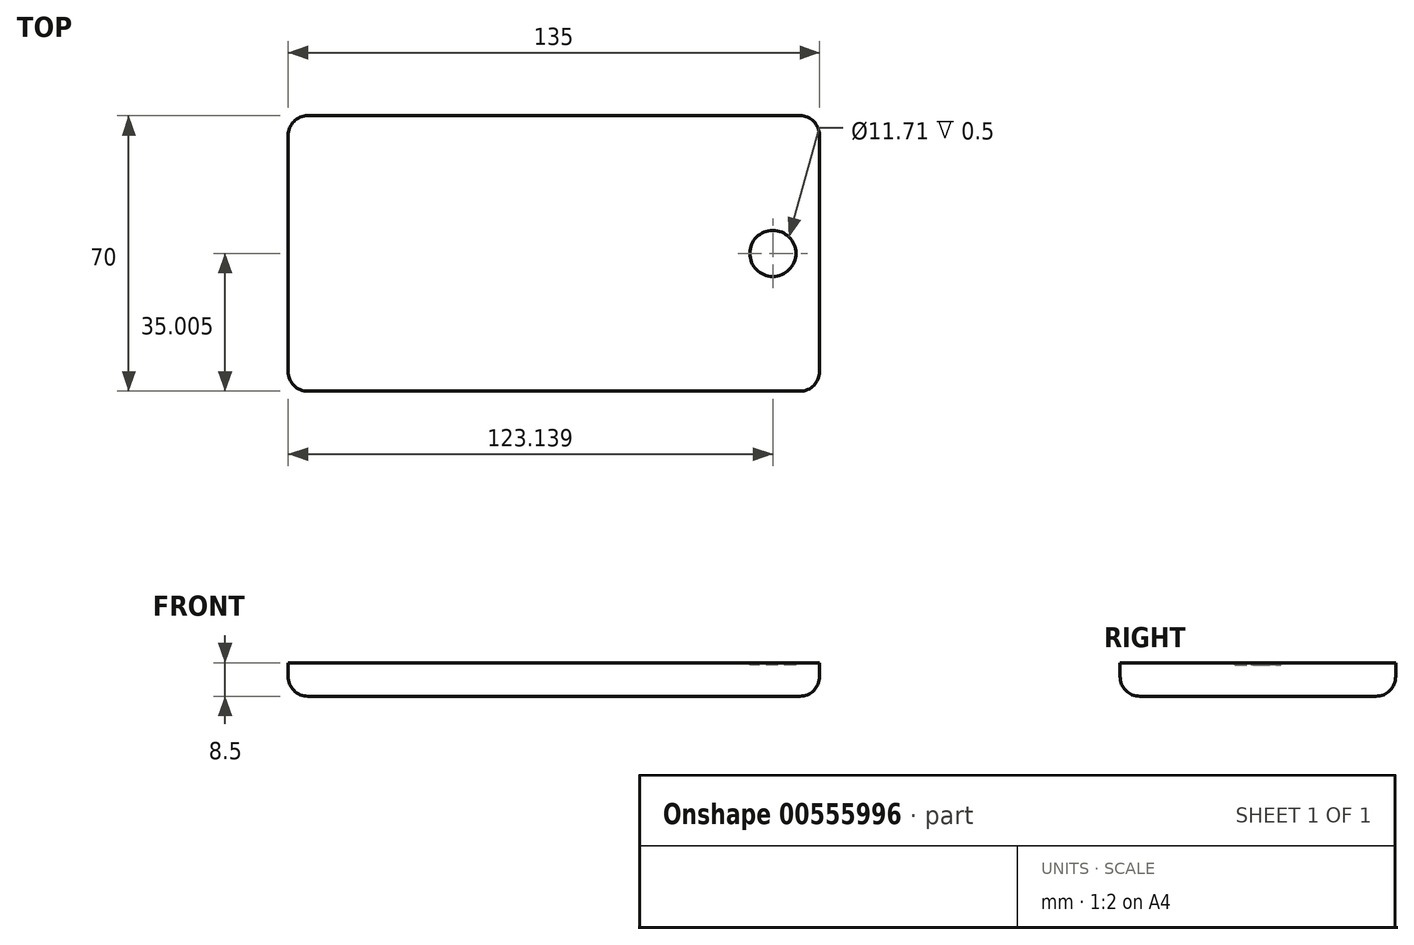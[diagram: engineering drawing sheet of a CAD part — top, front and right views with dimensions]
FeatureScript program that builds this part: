
annotation { "Feature Type Name" : "Feature", "Feature Type Description" : "" }
export const myFeature = defineFeature(function(context is Context, id is Id, definition is map)
    precondition{}
    {
        {
            var Q0;
            Q0=qCreatedBy(makeId("Top.planeOp"),FACE);
            var sketch = newSketch(context, id + "F0", { "sketchPlane" : qUnion([Q0])});
            skLineSegment(sketch, "E0.bottom", {"start": v(67.7, 57.37) * mm, "end": v(-67.3, 57.37) * mm});
            skLineSegment(sketch, "E0.top", {"start": v(67.7, -12.63) * mm, "end": v(-67.3, -12.63) * mm});
            skLineSegment(sketch, "E0.left", {"start": v(67.7, 57.37) * mm, "end": v(67.7, -12.63) * mm});
            skLineSegment(sketch, "E0.right", {"start": v(-67.3, 57.37) * mm, "end": v(-67.3, -12.63) * mm});
            skSolve(sketch);
        }
        {
            var Q0;
            Q0 = qSketchRegion(id + "F0", true);
            extrude(context, id + "F1", {"entities" : qUnion([Q0]), "depth" : 8.5 * mm, "offsetDistance" : 25 * mm});
        }
        {
            var Q0;
            Q0=makeQuery(id+"F1.opExtrude","SWEPT_EDGE",EDGE,{"disambiguationData":[OSD([sQuery(id+"F0.wireOp",EDGE,"E0.top"),sQuery(id+"F0.wireOp",EDGE,"E0.left")])]});
            var Q1;
            Q1=makeQuery(id+"F1.opExtrude","SWEPT_EDGE",EDGE,{"disambiguationData":[OSD([sQuery(id+"F0.wireOp",EDGE,"E0.bottom"),sQuery(id+"F0.wireOp",EDGE,"E0.left")])]});
            var Q2;
            Q2=makeQuery(id+"F1.opExtrude","SWEPT_EDGE",EDGE,{"disambiguationData":[OSD([sQuery(id+"F0.wireOp",EDGE,"E0.top"),sQuery(id+"F0.wireOp",EDGE,"E0.right")])]});
            var Q3;
            Q3=makeQuery(id+"F1.opExtrude","SWEPT_EDGE",EDGE,{"disambiguationData":[OSD([sQuery(id+"F0.wireOp",EDGE,"E0.bottom"),sQuery(id+"F0.wireOp",EDGE,"E0.right")])]});
            fillet(context, id + "F2", {"entities" : qUnion([Q0, Q1, Q2, Q3]), "radius" : 5 * mm, "tangentPropagation" : true, "allowEdgeOverflow" : false});
        }
        {
            var Q0;
            Q0=makeQuery(id+"F1.opExtrude","CAP_EDGE",EDGE,{"disambiguationData":[OSD([sQuery(id+"F0.wireOp",EDGE,"E0.right")])],"isStart":true});
            fillet(context, id + "F3", {"entities" : qUnion([Q0]), "radius" : 5 * mm, "tangentPropagation" : true, "allowEdgeOverflow" : false});
        }
        {
            var Q0;
            Q0=makeQuery(id+"F1.opExtrude","CAP_FACE",FACE,{"disambiguationData":[OSD([sQuery(id+"F0.wireOp",EDGE,"E0.bottom"),sQuery(id+"F0.wireOp",EDGE,"E0.top"),sQuery(id+"F0.wireOp",EDGE,"E0.left"),sQuery(id+"F0.wireOp",EDGE,"E0.right")])],"isStart":false});
            var sketch = newSketch(context, id + "F4", { "sketchPlane" : qUnion([Q0])});
            skCircle(sketch, "E1", {"center": v(55.85, 22.37) * mm, "radius": 5.85 * mm});
            skPoint(sketch, "E1.centerSnap0", {"position": v(67.7, 22.37) * mm});
            skSolve(sketch);
        }
        {
            var Q0;
            Q0=makeQuery(id+"F4.imprint","IMPRINT",FACE,{"disambiguationData":[TD([[makeQuery(id+"F4.imprint","IMPRINT",EDGE,{"derivedFrom":sQuery(id+"F4.wireOp",EDGE,"E1")}),1.0]])]});
            extrude(context, id + "F5", {"entities" : qUnion([Q0]), "operationType" : NewBodyOperationType.REMOVE, "oppositeDirection" : true, "depth" : 0.5 * mm, "offsetDistance" : 25 * mm});
        }
    });
